# Revit family: Sanitary_Showers_hansgrohe_26971CHN-Pulsify-S-Showerpipe_260_1jet_bath-thermostat_ShowerTablet-360
name_source: partatom
category: Plumbing Fixtures
units: mm (PartAtom-declared; Revit-internal decimal feet)

## family parameters
Cut with Voids When Loaded = Yes
Host = Face
Maintain Annotation Orientation = No
OmniClass Number = 23.31.17.00
OmniClass Title = Showers
Part Type = Normal
Room Calculation Point = No
Round Connector Dimension = Use Diameter
Shared = No

## types (3) — shared parameters
Connector Description = Water Inlet 12.70 mm
Description = Pulsify S Showerpipe 260 1jet with bath hermostat ShowerTablet 360
Diameter = 13  [stored 0.0426509 ft]
Manufacturer = Hansgrohe
Model = 26971CHN
Product Page URL = https://www.hansgrohe.com
Product data url = https://www.bimobject.com
URL = https://www.hansgrohe.com
Version = 1
zero-valued in all types: Default Elevation

## per-type parameters (varying)
| type | Material 1 |
| 007 Chrome | Hansgrohe - Metal - 007 Chrome |
| 707 Matt White | Hansgrohe - Metal - 707 Matt White |
| 677 Matte Black | Hansgrohe - Metal - 677 Matte Black |

note: [stored X ft] marks values corroborated as IEEE doubles in the binary element streams (Revit-internal decimal feet)

## geometry (parser evidence)
native form markers: Sweep x2
no freeform markers — native parametric forms only
